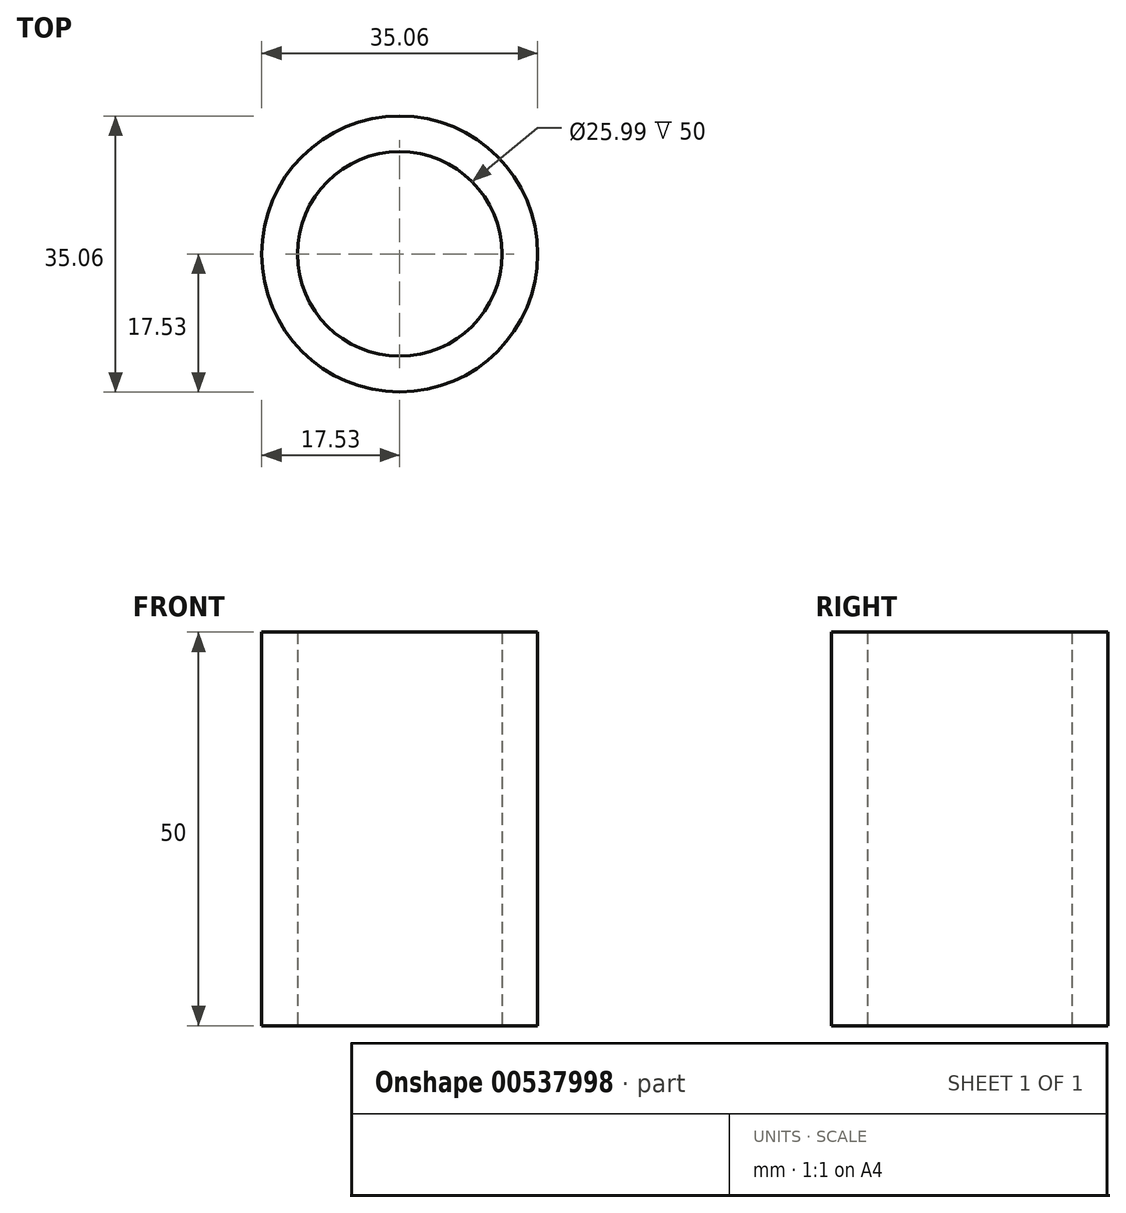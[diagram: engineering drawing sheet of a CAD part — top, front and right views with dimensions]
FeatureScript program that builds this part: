
annotation { "Feature Type Name" : "Feature", "Feature Type Description" : "" }
export const myFeature = defineFeature(function(context is Context, id is Id, definition is map)
    precondition{}
    {
        {
            var Q0;
            Q0=qCreatedBy(makeId("Top.planeOp"),FACE);
            var sketch = newSketch(context, id + "F0", { "sketchPlane" : qUnion([Q0])});
            skCircle(sketch, "E0", {"center": v(0, 0) * mm, "radius": 17.53 * mm});
            skCircle(sketch, "E1", {"center": v(0, 0) * mm, "radius": 13 * mm});
            skSolve(sketch);
        }
        {
            var Q0;
            Q0 = qSketchRegion(id + "F0", true);
            extrude(context, id + "F1", {"entities" : qUnion([Q0]), "depth" : 50 * mm, "offsetDistance" : 25 * mm});
        }
    });
